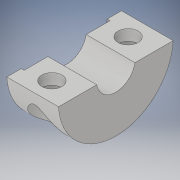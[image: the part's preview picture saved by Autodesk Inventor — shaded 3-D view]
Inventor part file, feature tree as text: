
AUTODESK INVENTOR PART (.ipt)
format: ipt  version: 2019 (Build 230136000, 136)  size: 180,736 bytes
history: native  units: mm
features: sketch x5, extrude x4, plane x2, hole x1, mirror x1
ambient origin geometry x8: Origin, YZ Plane, XZ Plane, XY Plane, X Axis, Y Axis, Z Axis, Center Point
bodies: Solid1 (feature_tree)
feature tree (13):
  extrude  "Extrusion1"  Depth=20.0mm
  extrude  "Extrusion3"  Depth=3.490659mm
  plane  "Work Plane1"
  extrude  "Extrusion4"  Depth=9.0mm
  plane  "Work Plane2"
  hole  "Hole1"  [1 undecoded]
  mirror  "Mirror1"
  extrude  "Extrusion6"  Depth=7.5mm TaperAngle=0.0deg
  sketch  "Sketch1"  dims[d0=6.75mm d1=20.0mm]
  sketch  "Sketch3"  dims[d2=13.962634mm d3=3.490659mm]
  sketch  "Sketch4"  dims[d4=9.0mm d5=0.0mm d9=15.0mm]
  sketch  "Sketch5"  dims[d10=0.5mm d11=0.0mm d12=10.0mm]
  sketch  "Sketch9"  dims[d13=5.5mm d14=7.5mm d15=0.0mm d16=-20.0mm d17=3.5mm d18=6.0mm d19=6.0mm d20=7.5mm d21=90.0deg d22=8.0mm d23=0.0mm d29=10.0mm d30=0.0mm]
note: 1 required parameter value undecoded (feature->parameter linkage not recoverable at this tier; creation-order binding heuristic only, values carry confidence <= 0.55)
